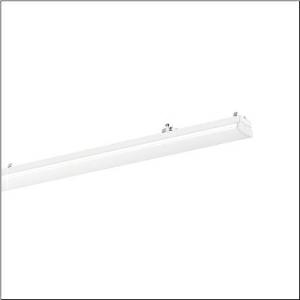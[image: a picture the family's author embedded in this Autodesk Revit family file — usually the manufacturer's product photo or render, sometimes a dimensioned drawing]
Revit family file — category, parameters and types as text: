
# Revit family: licross_11_recessed_opal_mo_51te1ddn445g
name_source: partatom
category: Lighting Fixtures
units: mm (PartAtom-declared; Revit-internal decimal feet)

## family parameters
Cut with Voids When Loaded = No
Host = Face
Light Source = No
Part Type = Normal
Room Calculation Point = No
Round Connector Dimension = Use Diameter
Shared = No

## types (1)
- --- (1 x LED, 4500 lm, 25.2 W, 4000K)
    Apparent Load = 25 VA
    CIE Flux Codes = 44 73 91 87 100
    Color Rendering = 80
    Color Temperature = 4000K
    Default Elevation = 1800 mm
    Description = Licross 11 recessed opal MO, luminaire insert, of sheet steel, coil coated, white, length: 1.500mm, width: 76mm, height: 87mm, LED rated luminous flux: 4.500lm, light colour: 840, SDCM (Standard Deviation of Colour Matching)MacAdam ≤ 2 SDCM (initial), control gear: DALI 2, with plug, 5-pole, with phase selection, mains connection: 220..240V, AC, 50/60Hz, rated input power: 25W, internal wiring halogen-free, primary optical cover: cover, of PMMA, light emission: direct with ceiling illumination distribution, primary light characteristic: symmetric, protection rating (complete): IP54, insulation class (complete): insulation class I (protective earthing), certification: CE, ENEC, VDE, UKCA, protection symbol: D if used in an environment with non-conductive dust loads with corresponding accessories, impact resistance: IK06, permissible ambient temperature for indoor applications: -25..+45°C, corresponds to IFS (International Featured Standards) requirements for safety and quality in the food industry, reducing of maximum allowable ambient temperature of 5°C with ceiling mounting, LABS conformity tested according to VDMA 24364:2018-05, The light source and the operating device comply with the requirements of the Ecodesign Regulation (EU) 2019/2020 and are replaceable in accordance with this regulation, packaging unit: 1 piece
    Height = 83 mm
    Lamp = 1 x LED
    Lamp Light Flux = 4500 lm
    Lamp Power = 25.2 W
    Lamp count = 1
    Length = 1500 mm
    Luminous efficacy = 179 lm/W
    Manufacturer = Siteco
    ModVariant = No
    Model = 51TE1DDN445G
    Mounting Place = Ceiling
    Mounting Type = Pendant
    Number of Poles = 1
    OnlyDefault = Yes
    Power Factor = 1
    Product Name = Licross 11 recessed opal MO
    Product group = luminaire insert | ceiling pendant
    ProductGroupID = 901
    Protection Class = Protection class I
    Protection Degree = IP 54
    RLX_Detail_Level = 1
    RLX_Emergency_Light_Flux = 0 lm
    RLX_Emergency_Type = 0
    RLX_Emergency_Type_DB = No
    RlxData = <blob elided: 26857 chars, md5=1cf86189>
    Socket = socket
    Standby Power = 0 W
    System Light Flux = 4500 lm
    System Power = 25 W
    Type Comments = factory setting: luminous flux: 100 % | dim-lin: 254 | 167 mA
    Type Image = l_1313666.jpg
    URL = http://relux.com
    VarID = @adj_083769
    Voltage = 0 V
    Weight = 0.00 kg
    Width = 76 mm

## geometry (parser evidence)
native form markers: Blend x4, Sweep x12
no freeform markers — native parametric forms only
